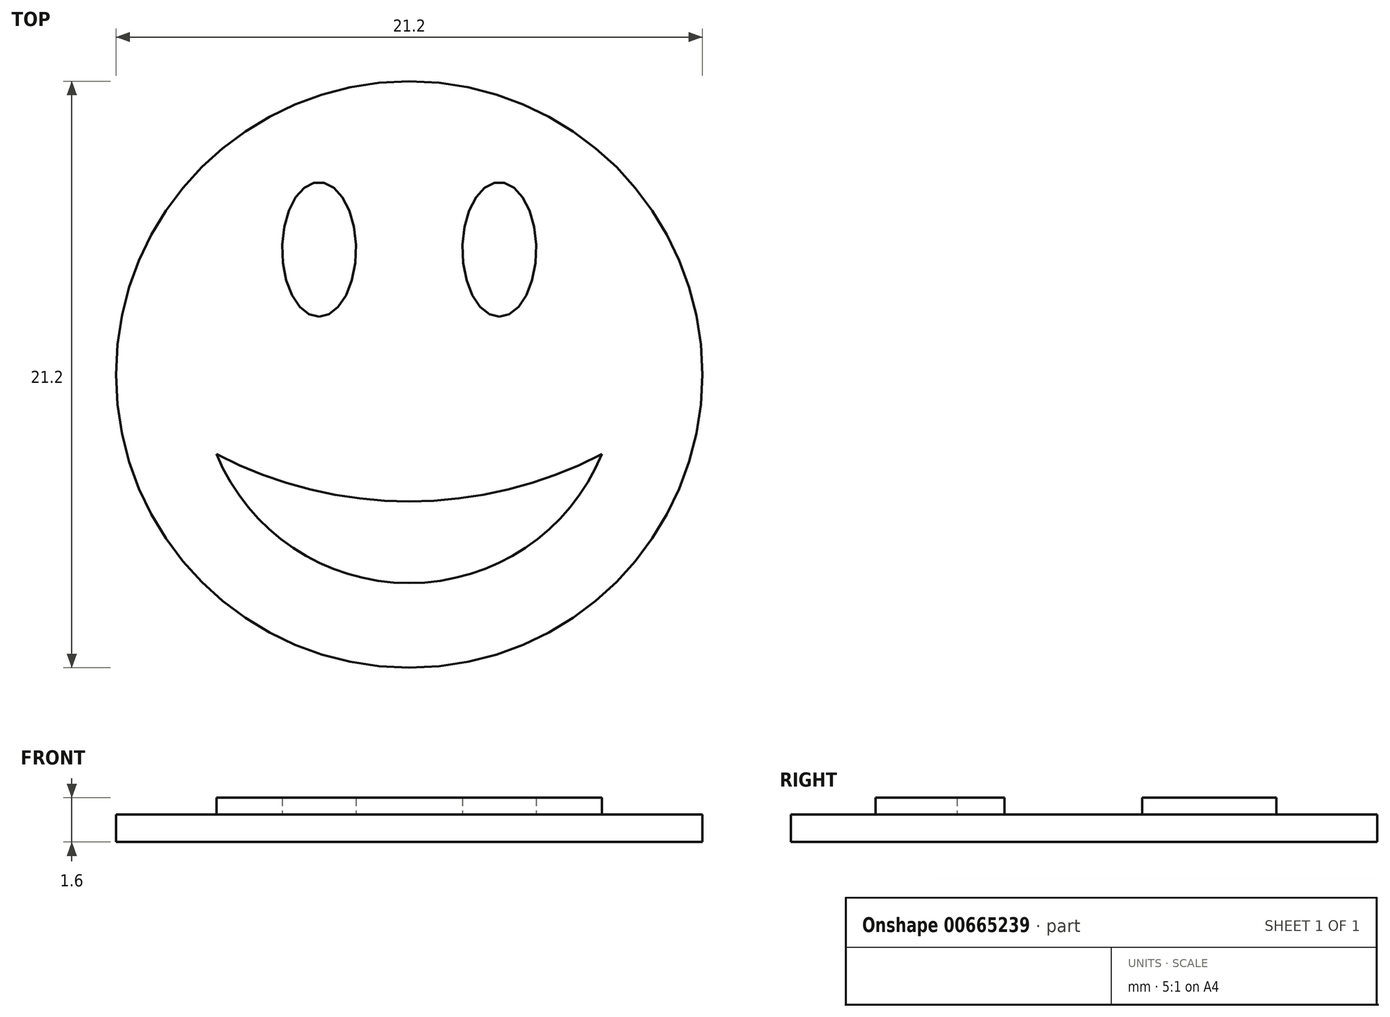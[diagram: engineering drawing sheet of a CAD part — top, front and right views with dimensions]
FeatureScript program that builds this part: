
annotation { "Feature Type Name" : "Feature", "Feature Type Description" : "" }
export const myFeature = defineFeature(function(context is Context, id is Id, definition is map)
    precondition{}
    {
        {
            var Q0;
            Q0=qCreatedBy(makeId("Top.planeOp"),FACE);
            var sketch = newSketch(context, id + "F0", { "sketchPlane" : qUnion([Q0])});
            skCircle(sketch, "E0", {"center": v(0, 0) * mm, "radius": 10.6 * mm});
            skSolve(sketch);
        }
        {
            var Q0;
            Q0 = qSketchRegion(id + "F0", true);
            extrude(context, id + "F1", {"entities" : qUnion([Q0]), "depth" : 1 * mm, "offsetDistance" : 25 * mm});
        }
        {
            var Q0;
            Q0=makeQuery(id+"F1.opExtrude","CAP_FACE",FACE,{"disambiguationData":[OSD([sQuery(id+"F0.wireOp",EDGE,"E0")])],"isStart":false});
            var sketch = newSketch(context, id + "F2", { "sketchPlane" : qUnion([Q0])});
            skArc(sketch, "E1", {"start": v(0, -7.54) * mm, "mid": v(-4.2, -6.27) * mm, "end": v(-6.97, -2.88) * mm});
            skArc(sketch, "E2.MirrorCS", {"start": v(0, -7.54) * mm, "mid": v(4.2, -6.27) * mm, "end": v(6.97, -2.88) * mm});
            skArc(sketch, "E3", {"start": v(-6.97, -2.88) * mm, "mid": v(0, -4.59) * mm, "end": v(6.97, -2.88) * mm});
            skEllipse(sketch, "E4", {"center": v(-3.26, 4.52) * mm, "majorRadius": 2.43 * mm, "minorRadius": 1.34 * mm, "majorAxis": v(0, -1)});
            skEllipse(sketch, "E5.MirrorC", {"center": v(3.26, 4.52) * mm, "majorRadius": 2.43 * mm, "minorRadius": 1.34 * mm, "majorAxis": v(0, -1)});
            skSolve(sketch);
        }
        {
            var Q0;
            Q0 = qSketchRegion(id + "F2", true);
            extrude(context, id + "F3", {"entities" : qUnion([Q0]), "operationType" : NewBodyOperationType.ADD, "depth" : .6 * mm, "offsetDistance" : 25 * mm});
        }
    });
